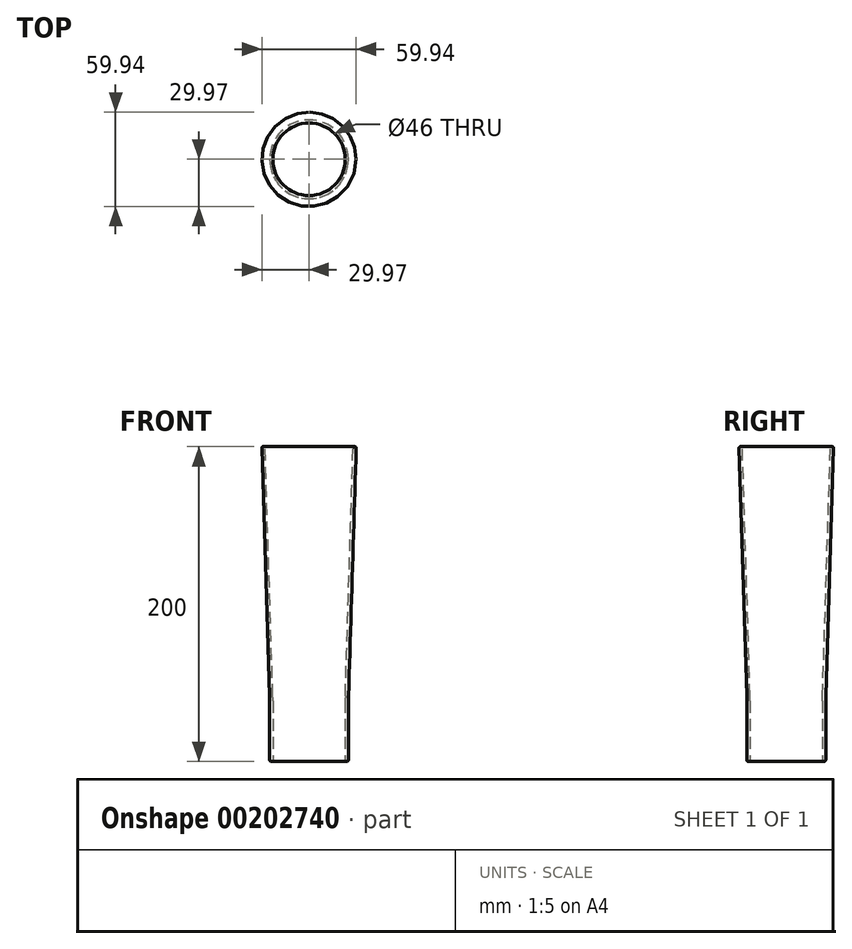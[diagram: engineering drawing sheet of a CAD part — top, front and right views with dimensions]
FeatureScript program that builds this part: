
annotation { "Feature Type Name" : "Feature", "Feature Type Description" : "" }
export const myFeature = defineFeature(function(context is Context, id is Id, definition is map)
    precondition{}
    {
        {
            var Q0;
            Q0=qCreatedBy(makeId("Front.planeOp"),FACE);
            var sketch = newSketch(context, id + "F0", { "sketchPlane" : qUnion([Q0])});
            skLineSegment(sketch, "E0", {"start": v(0, -154.16) * mm, "end": v(0, 45.84) * mm});
            skLineSegment(sketch, "E1", {"start": v(-28, 45.84) * mm, "end": v(-30, 45.84) * mm});
            skLineSegment(sketch, "E2", {"start": v(-30, 45.84) * mm, "end": v(-25, -114.16) * mm});
            skLineSegment(sketch, "E3", {"start": v(-25, -114.16) * mm, "end": v(-25, -154.16) * mm});
            skLineSegment(sketch, "E4", {"start": v(-25, -154.16) * mm, "end": v(-23, -154.16) * mm});
            skLineSegment(sketch, "E5.0", {"start": v(-23, -114.13) * mm, "end": v(-23, -154.16) * mm});
            skLineSegment(sketch, "E5.1", {"start": v(-28, 45.9) * mm, "end": v(-23, -114.13) * mm});
            skSolve(sketch);
        }
        {
            var Q0;
            Q0 = qSketchRegion(id + "F0", true);
            var Q1;
            Q1=sQuery(id+"F0.wireOp",EDGE,"E0");
            revolve(context, id + "F1", {"entities" : qUnion([Q0]), "axis" : qUnion([Q1]), "revolveType" : RevolveType.FULL});
        }
        {
            var Q0;
            Q0=makeQuery(id+"F1.opRevolve","SWEPT_EDGE",EDGE,{"disambiguationData":[OSD([sQuery(id+"F0.wireOp",EDGE,"E2"),sQuery(id+"F0.wireOp",EDGE,"E3")])]});
            var Q1;
            Q1=makeQuery(id+"F1.opRevolve","SWEPT_EDGE",EDGE,{"disambiguationData":[OSD([sQuery(id+"F0.wireOp",EDGE,"E5.0"),sQuery(id+"F0.wireOp",EDGE,"E5.1")])]});
            fillet(context, id + "F2", {"entities" : qUnion([Q0, Q1]), "radius" : 100 * mm, "tangentPropagation" : true, "allowEdgeOverflow" : false});
        }
        {
            var Q0;
            Q0=makeQuery(id+"F1.opRevolve","SWEPT_FACE",FACE,{"disambiguationData":[OSD([sQuery(id+"F0.wireOp",EDGE,"E1")])]});
            var Q1;
            Q1=makeQuery(id+"F1.opRevolve","SWEPT_FACE",FACE,{"disambiguationData":[OSD([sQuery(id+"F0.wireOp",EDGE,"E4")])]});
            fillet(context, id + "F3", {"entities" : qUnion([Q0, Q1]), "radius" : 1 * mm, "tangentPropagation" : true, "allowEdgeOverflow" : false});
        }
    });
